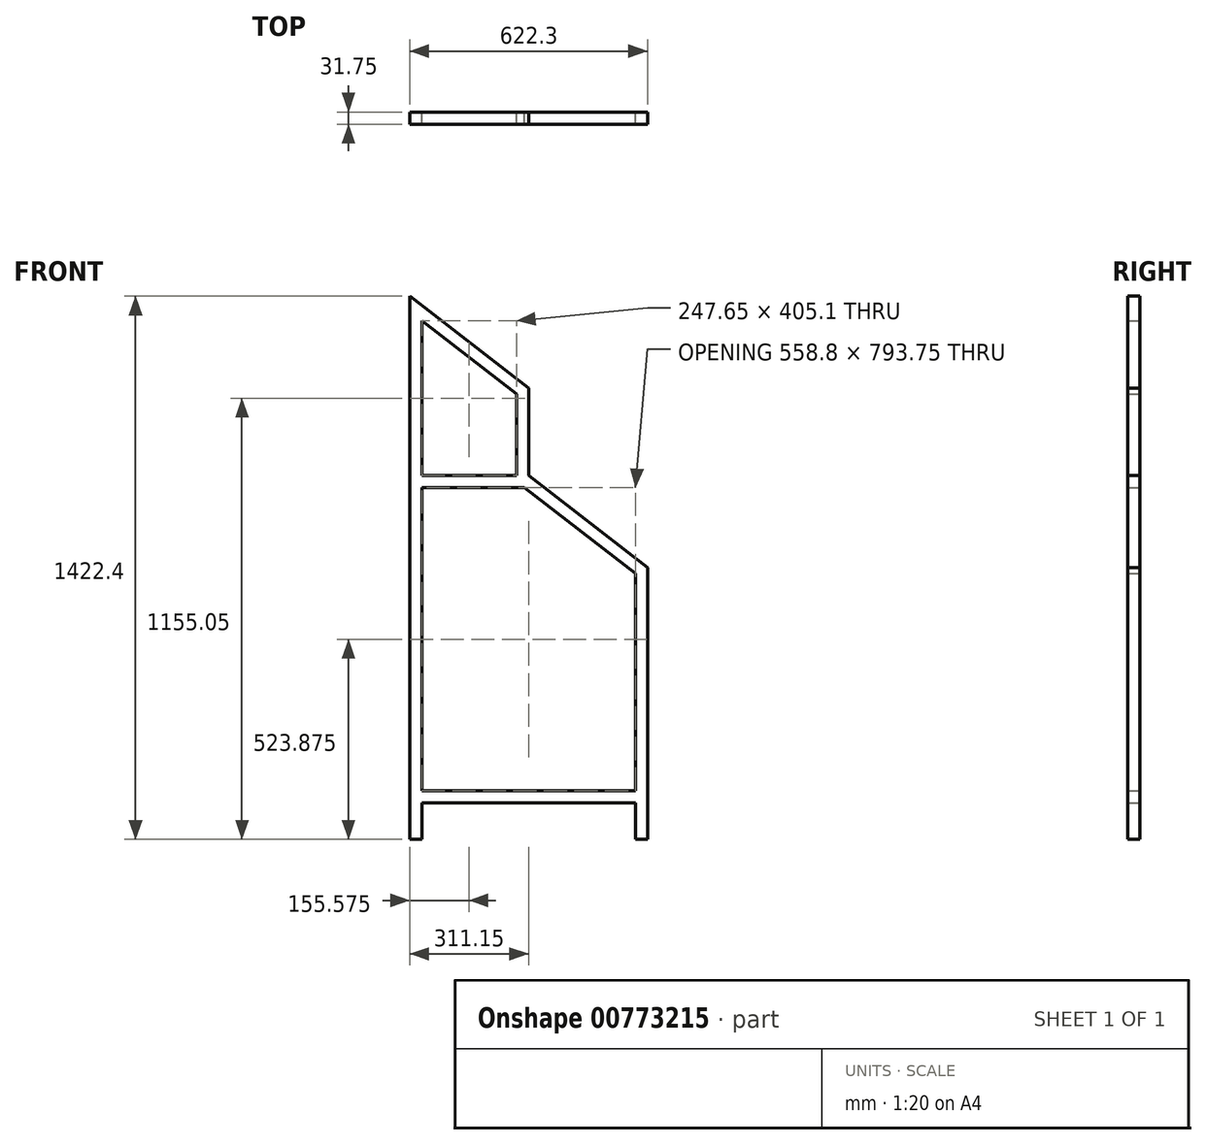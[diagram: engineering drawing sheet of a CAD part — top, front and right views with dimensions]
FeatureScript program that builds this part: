
annotation { "Feature Type Name" : "Feature", "Feature Type Description" : "" }
export const myFeature = defineFeature(function(context is Context, id is Id, definition is map)
    precondition{}
    {
        {
            var Q0;
            Q0=qCreatedBy(makeId("Front.planeOp"),FACE);
            var sketch = newSketch(context, id + "F0", { "sketchPlane" : qUnion([Q0])});
            skLineSegment(sketch, "E0", {"start": v(0, 0) * mm, "end": v(0, 1422.4) * mm});
            skLineSegment(sketch, "E1", {"start": v(0, 0) * mm, "end": v(31.75, 0) * mm});
            skLineSegment(sketch, "E2", {"start": v(622.3, 0) * mm, "end": v(622.3, 711.2) * mm});
            skLineSegment(sketch, "E3", {"start": v(0, 952.5) * mm, "end": v(0, 711.2) * mm});
            skLineSegment(sketch, "E4", {"start": v(311.15, 952.5) * mm, "end": v(622.3, 711.2) * mm});
            skLineSegment(sketch, "E5", {"start": v(311.15, 952.5) * mm, "end": v(311.15, 1181.1) * mm});
            skLineSegment(sketch, "E6", {"start": v(0, 1422.4) * mm, "end": v(311.15, 1181.1) * mm});
            skLineSegment(sketch, "E7.0", {"start": v(590.55, 0) * mm, "end": v(590.55, 695.64) * mm});
            skLineSegment(sketch, "E7.1", {"start": v(31.75, 0) * mm, "end": v(31.75, 1357.6) * mm});
            skLineSegment(sketch, "E7.2", {"start": v(31.75, 1357.6) * mm, "end": v(279.4, 1165.54) * mm});
            skLineSegment(sketch, "E7.3", {"start": v(279.4, 952.5) * mm, "end": v(279.4, 1165.54) * mm});
            skLineSegment(sketch, "E7.4", {"start": v(300.28, 920.75) * mm, "end": v(590.55, 695.64) * mm});
            skLineSegment(sketch, "E8.trimOffspring", {"start": v(590.55, 0) * mm, "end": v(622.3, 0) * mm});
            skLineSegment(sketch, "E9", {"start": v(311.15, 952.5) * mm, "end": v(31.75, 952.5) * mm});
            skLineSegment(sketch, "E10.0", {"start": v(300.28, 920.75) * mm, "end": v(31.75, 920.75) * mm});
            skLineSegment(sketch, "E11", {"start": v(31.75, 127) * mm, "end": v(590.55, 127) * mm});
            skLineSegment(sketch, "E12.0", {"start": v(31.75, 95.25) * mm, "end": v(590.55, 95.25) * mm});
            skSolve(sketch);
        }
        {
            var Q0;
            {var subQ6=sQuery(id+"F0.wireOp",EDGE,"E1");Q0=makeQuery(id+"F0.imprint","IMPRINT",FACE,{"disambiguationData":[TD([[makeQuery(id+"F0.imprint","IMPRINT",EDGE,{"derivedFrom":subQ6}),1.0]])]});}
            var Q1;
            Q1=makeQuery(id+"F0.imprint","IMPRINT",FACE,{"disambiguationData":[TD([[makeQuery(id+"F0.imprint","IMPRINT",EDGE,{"derivedFrom":sQuery(id+"F0.wireOp",EDGE,"E2")}),1.0]])]});
            var Q2;
            {var subQ0=sQuery(id+"F0.wireOp",EDGE,"E11");Q2=makeQuery(id+"F0.imprint","IMPRINT",FACE,{"disambiguationData":[TD([[makeQuery(id+"F0.imprint","IMPRINT",EDGE,{"derivedFrom":subQ0}),-1.0]])]});}
            extrude(context, id + "F1", {"entities" : qUnion([Q0, Q1, Q2]), "depth" : 31.75 * mm, "offsetDistance" : 25.4 * mm});
        }
    });
